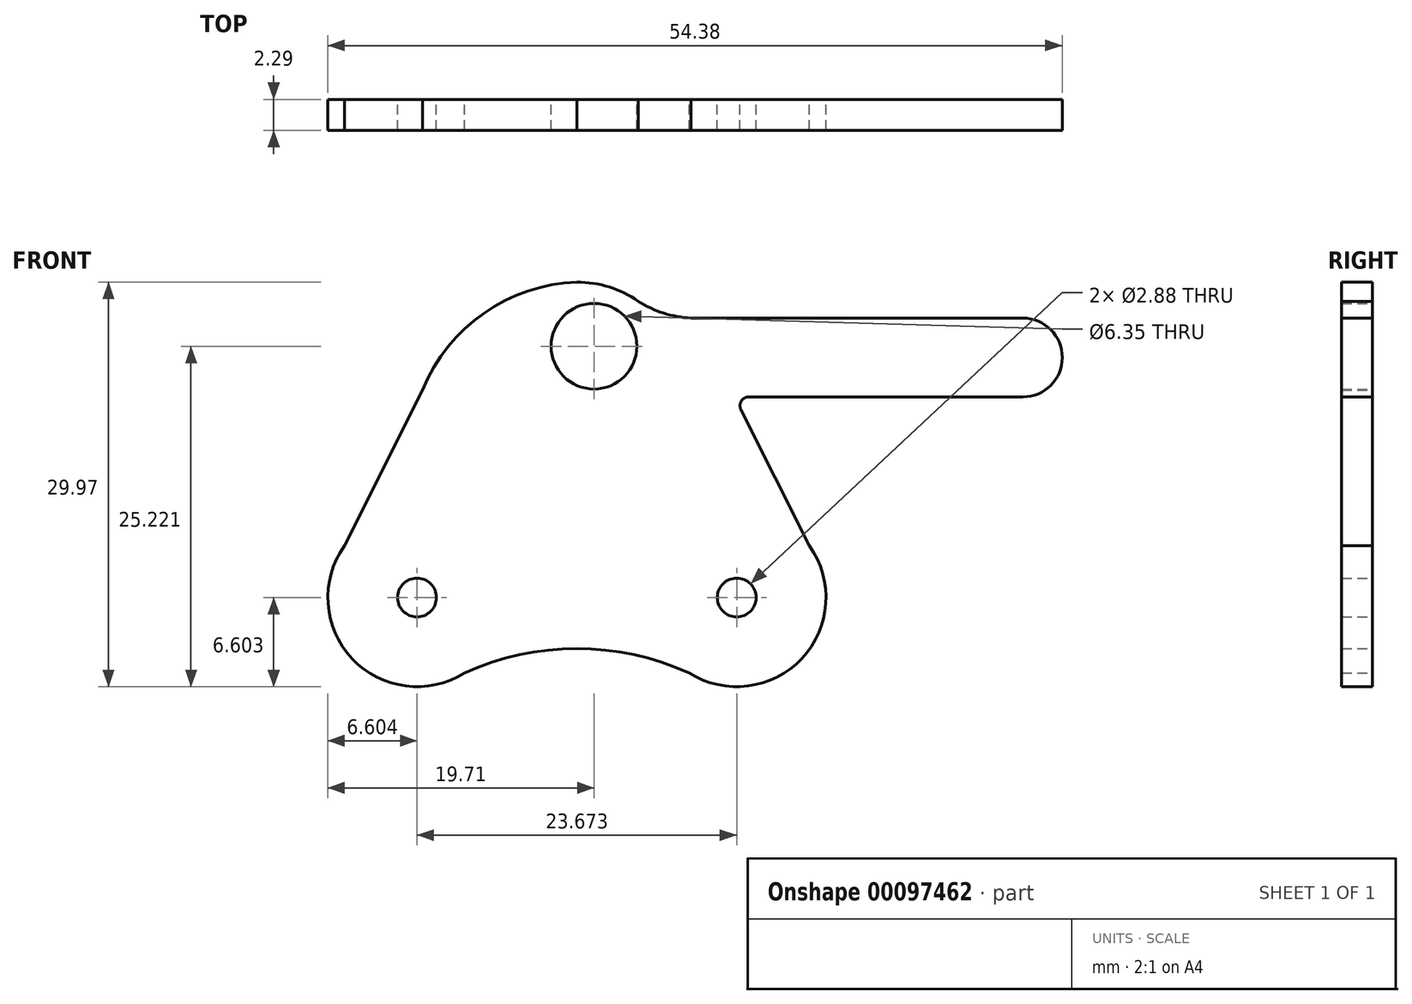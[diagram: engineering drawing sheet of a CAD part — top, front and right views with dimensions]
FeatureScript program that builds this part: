
annotation { "Feature Type Name" : "Feature", "Feature Type Description" : "" }
export const myFeature = defineFeature(function(context is Context, id is Id, definition is map)
    precondition{}
    {
        {
            var Q0;
            Q0=qCreatedBy(makeId("Front.planeOp"),FACE);
            var sketch = newSketch(context, id + "F0", { "sketchPlane" : qUnion([Q0])});
            skCircle(sketch, "E0", {"center": v(-11.84, -15.37) * mm, "radius": 1.44 * mm});
            skCircle(sketch, "E1", {"center": v(11.84, -15.37) * mm, "radius": 1.44 * mm});
            skLineSegment(sketch, "E2", {"start": v(0, 8) * mm, "end": v(0, -25.62) * mm, "construction": true});
            skArc(sketch, "E3", {"start": v(-17.21, -11.53) * mm, "mid": v(-16.64, -19.9) * mm, "end": v(-8.32, -20.96) * mm});
            skArc(sketch, "E4", {"start": v(8.32, -20.96) * mm, "mid": v(16.64, -19.9) * mm, "end": v(17.21, -11.53) * mm});
            skLineSegment(sketch, "E5", {"start": v(-11.84, -21.97) * mm, "end": v(11.84, -21.97) * mm, "construction": true});
            skLineSegment(sketch, "E6", {"start": v(-6.44, -19.18) * mm, "end": v(6.44, -19.18) * mm, "construction": true});
            skLineSegment(sketch, "E7", {"start": v(-8.32, -20.96) * mm, "end": v(8.32, -20.96) * mm, "construction": true});
            skLineSegment(sketch, "E8", {"start": v(0, 2.41) * mm, "end": v(43.51, 2.41) * mm, "construction": true});
            skArc(sketch, "E9", {"start": v(33.02, -0.5) * mm, "mid": v(35.94, 2.41) * mm, "end": v(33.02, 5.33) * mm});
            skCircle(sketch, "E10", {"center": v(1.27, 3.25) * mm, "radius": 3.18 * mm});
            skArc(sketch, "E11", {"start": v(8.32, -20.96) * mm, "mid": v(0, -19.15) * mm, "end": v(-8.32, -20.96) * mm});
            skLineSegment(sketch, "E12", {"start": v(-17.21, -11.53) * mm, "end": v(-11.43, 0) * mm});
            skLineSegment(sketch, "E13", {"start": v(17.21, -11.53) * mm, "end": v(12.15, -1.43) * mm});
            skArc(sketch, "E14", {"start": v(4.54, 6.59) * mm, "mid": v(1.66, 7.83) * mm, "end": v(-1.47, 7.86) * mm});
            skLineSegment(sketch, "E15", {"start": v(33.02, 5.33) * mm, "end": v(8.44, 5.33) * mm});
            skLineSegment(sketch, "E16", {"start": v(33.02, -0.5) * mm, "end": v(12.71, -0.5) * mm});
            skPoint(sketch, "E17.orphan", {"position": v(11.43, 0) * mm});
            skPoint(sketch, "E18.visualSharp", {"position": v(11.69, -0.5) * mm});
            skArc(sketch, "E18.filletArc", {"start": v(12.71, -0.5) * mm, "mid": v(12.17, -0.81) * mm, "end": v(12.15, -1.43) * mm});
            skArc(sketch, "E19", {"start": v(4.54, 6.59) * mm, "mid": v(6.4, 5.7) * mm, "end": v(8.44, 5.33) * mm});
            skArc(sketch, "E20", {"start": v(0, 8) * mm, "mid": v(-6.9, 5.7) * mm, "end": v(-11.43, 0) * mm});
            skSolve(sketch);
        }
        {
            var Q0;
            Q0=makeQuery(id+"F0.imprint","IMPRINT",FACE,{"disambiguationData":[TD([[makeQuery(id+"F0.imprint","IMPRINT",EDGE,{"derivedFrom":sQuery(id+"F0.wireOp",EDGE,"E0")}),-1.0]])]});
            extrude(context, id + "F1", {"entities" : qUnion([Q0]), "depth" : 2.3 * mm});
        }
    });
